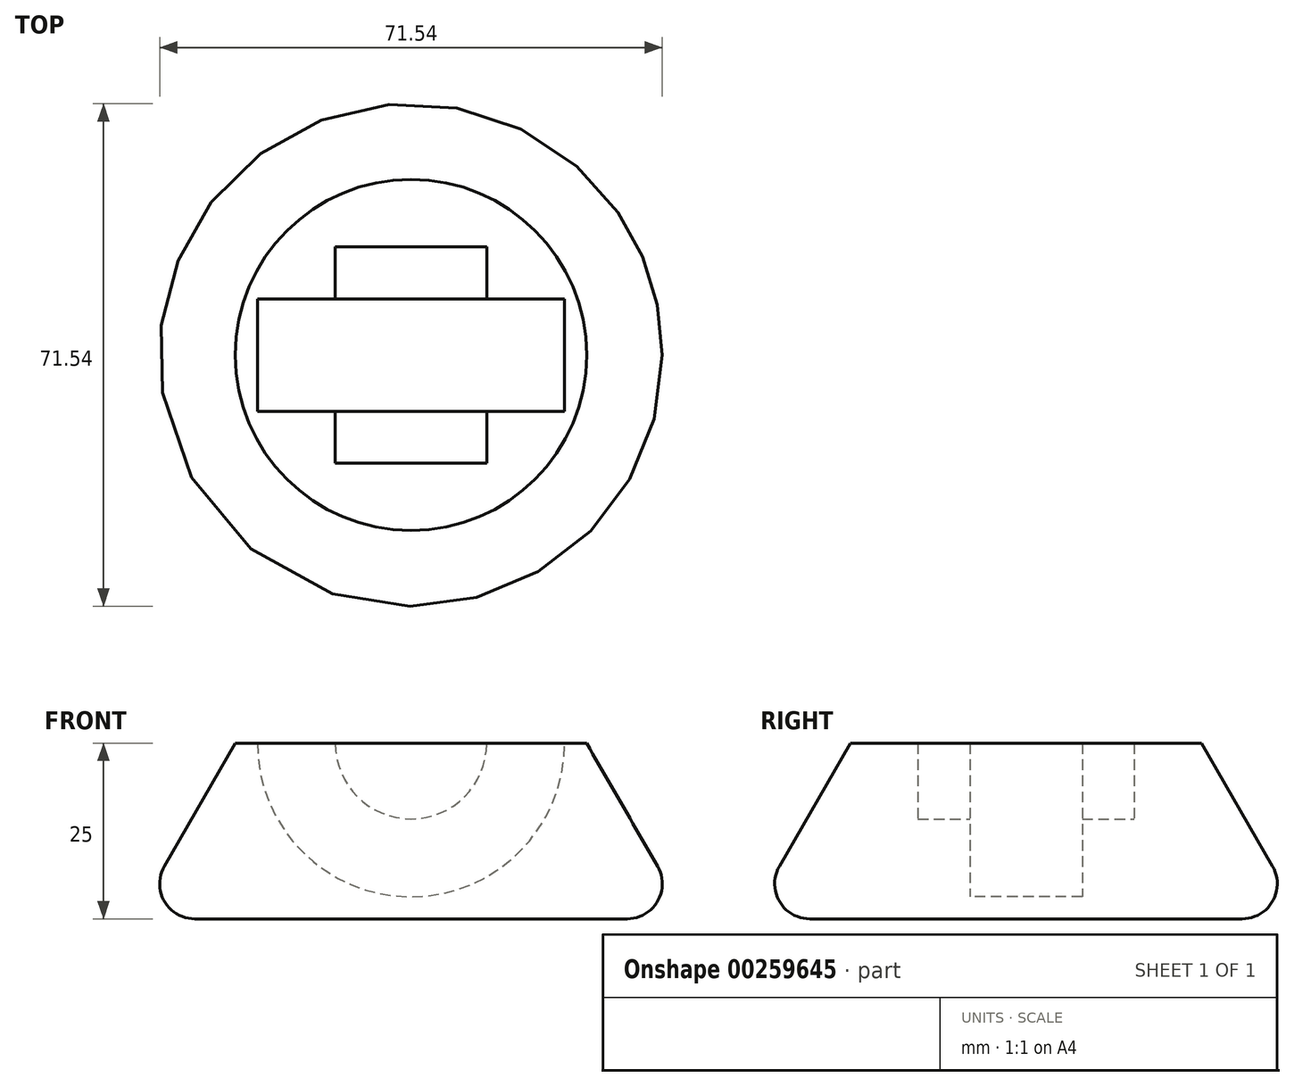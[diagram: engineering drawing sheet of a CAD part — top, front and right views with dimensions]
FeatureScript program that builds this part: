
annotation { "Feature Type Name" : "Feature", "Feature Type Description" : "" }
export const myFeature = defineFeature(function(context is Context, id is Id, definition is map)
    precondition{}
    {
        {
            assignVariable(context, id + "F0", {"name" : "casterwidth", "anyValue" : 15.4});
        }
        {
            var Q0;
            Q0=qCreatedBy(makeId("Front.planeOp"),FACE);
            var sketch = newSketch(context, id + "F1", { "sketchPlane" : qUnion([Q0])});
            skLineSegment(sketch, "E0", {"start": v(0, 0) * mm, "end": v(-39.43, 0) * mm});
            skLineSegment(sketch, "E1", {"start": v(-39.43, 0) * mm, "end": v(-25, 25) * mm});
            skLineSegment(sketch, "E2", {"start": v(-25, 25) * mm, "end": v(0, 25) * mm});
            skLineSegment(sketch, "E3", {"start": v(0, 25) * mm, "end": v(0, 0) * mm});
            skSolve(sketch);
        }
        {
            var Q0;
            Q0 = qSketchRegion(id + "F1", true);
            var Q1;
            Q1=sQuery(id+"F1.wireOp",EDGE,"E3");
            revolve(context, id + "F2", {"entities" : qUnion([Q0]), "axis" : qUnion([Q1]), "revolveType" : RevolveType.FULL});
        }
        {
            var Q0;
            Q0=qCreatedBy(makeId("Front.planeOp"),FACE);
            var sketch = newSketch(context, id + "F3", { "sketchPlane" : qUnion([Q0])});
            skLineSegment(sketch, "E4.0", {"start": v(-25, 25) * mm, "end": v(25, 25) * mm, "construction": true});
            skLineSegment(sketch, "E5", {"start": v(0, 25) * mm, "end": v(0, 3.15) * mm});
            skArc(sketch, "E6", {"start": v(-21.86, 25) * mm, "mid": v(0, 3.15) * mm, "end": v(21.86, 25) * mm});
            skLineSegment(sketch, "E7", {"start": v(-21.86, 25) * mm, "end": v(21.86, 25) * mm});
            skSolve(sketch);
        }
        {
            var Q0;
            Q0 = qSketchRegion(id + "F3", true);
            extrude(context, id + "F4", {"entities" : qUnion([Q0]), "operationType" : NewBodyOperationType.REMOVE, "endBound" : BoundingType.SYMMETRIC, "oppositeDirection" : true, "depth" : (getVariable(context, 'casterwidth') + 0.6) * mm});
        }
        {
            var Q0;
            Q0=makeQuery(id+"F2.opRevolve","SWEPT_EDGE",EDGE,{"disambiguationData":[OSD([sQuery(id+"F1.wireOp",EDGE,"E0"),sQuery(id+"F1.wireOp",EDGE,"E1")])]});
            fillet(context, id + "F5", {"entities" : qUnion([Q0]), "radius" : 5 * mm, "tangentPropagation" : true, "allowEdgeOverflow" : false});
        }
        {
            var Q0;
            Q0=qCreatedBy(makeId("Front.planeOp"),FACE);
            var sketch = newSketch(context, id + "F6", { "sketchPlane" : qUnion([Q0])});
            skLineSegment(sketch, "E8.0", {"start": v(-21.86, 25) * mm, "end": v(21.86, 25) * mm, "construction": true});
            skCircle(sketch, "E9", {"center": v(0, 25) * mm, "radius": 10.78 * mm});
            skSolve(sketch);
        }
        {
            var Q0;
            Q0 = qSketchRegion(id + "F6", true);
            extrude(context, id + "F7", {"entities" : qUnion([Q0]), "operationType" : NewBodyOperationType.REMOVE, "endBound" : BoundingType.SYMMETRIC, "depth" : (getVariable(context, 'casterwidth') * 2) * mm});
        }
    });
